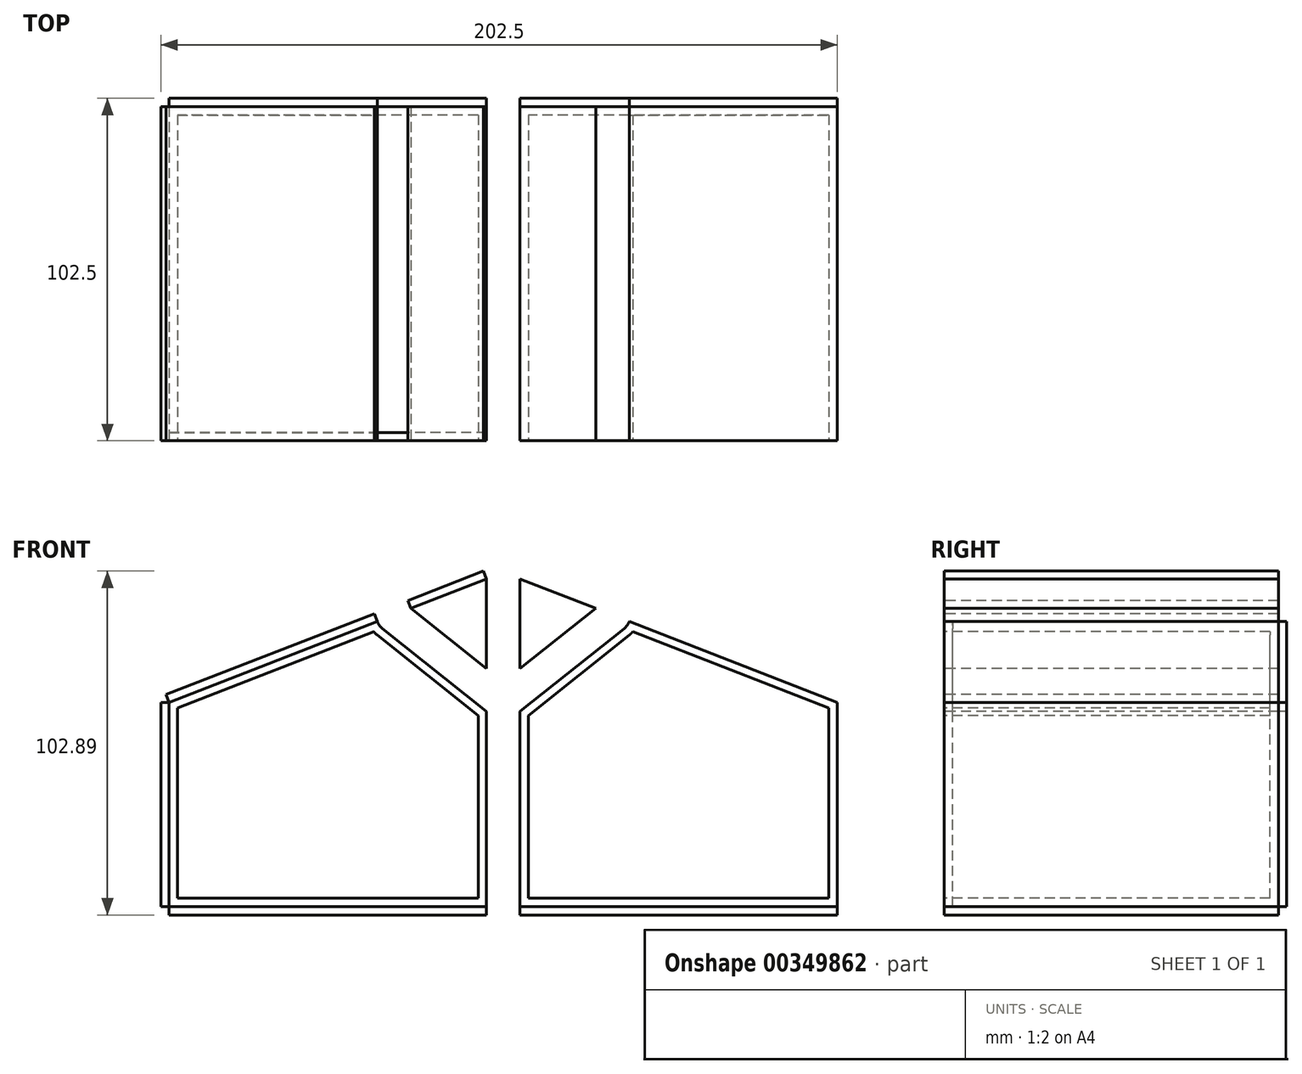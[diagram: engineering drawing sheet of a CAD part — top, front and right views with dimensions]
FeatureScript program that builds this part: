
annotation { "Feature Type Name" : "Feature", "Feature Type Description" : "" }
export const myFeature = defineFeature(function(context is Context, id is Id, definition is map)
    precondition{}
    {
        {
            var Q0;
            Q0=qCreatedBy(makeId("Front.planeOp"),FACE);
            var sketch = newSketch(context, id + "F0", { "sketchPlane" : qUnion([Q0])});
            skLineSegment(sketch, "E0", {"start": v(-100, 0) * mm, "end": v(-100, 61.13) * mm});
            skLineSegment(sketch, "E1", {"start": v(-100, 61.13) * mm, "end": v(0, 100) * mm});
            skLineSegment(sketch, "E2", {"start": v(0, 100) * mm, "end": v(100, 61.13) * mm});
            skLineSegment(sketch, "E3", {"start": v(100, 61.13) * mm, "end": v(100, 0) * mm});
            skLineSegment(sketch, "E4", {"start": v(100, 0) * mm, "end": v(-100, 0) * mm});
            skArc(sketch, "E5.0.endCap", {"start": v(-36.18, 83.24) * mm, "mid": v(-37.1, 84.18) * mm, "end": v(-37.72, 85.34) * mm});
            skLineSegment(sketch, "E5.0.left", {"start": v(-5, 58.4) * mm, "end": v(-36.18, 83.24) * mm});
            skArc(sketch, "E5.1.startCap", {"start": v(37.72, 85.34) * mm, "mid": v(37.1, 84.18) * mm, "end": v(36.18, 83.24) * mm});
            skLineSegment(sketch, "E5.1.left", {"start": v(36.18, 83.24) * mm, "end": v(5, 58.4) * mm});
            skLineSegment(sketch, "E5.1.right", {"start": v(27.67, 89.24) * mm, "end": v(5, 71.18) * mm});
            skLineSegment(sketch, "E5.2.left", {"start": v(-5, 0) * mm, "end": v(-5, 58.4) * mm});
            skLineSegment(sketch, "E5.2.right", {"start": v(5, 0) * mm, "end": v(5, 58.4) * mm});
            skLineSegment(sketch, "E6.trimOffspring", {"start": v(-5, 71.18) * mm, "end": v(-5, 98.06) * mm});
            skLineSegment(sketch, "E7.trimOffspring", {"start": v(-5, 71.18) * mm, "end": v(-27.67, 89.24) * mm});
            skLineSegment(sketch, "E8.trimOffspring", {"start": v(5, 71.18) * mm, "end": v(5, 98.06) * mm});
            skPoint(sketch, "E5.0.startCap.center.orphan", {"position": v(0, 60.8) * mm});
            skSolve(sketch);
        }
        {
            var Q0;
            {var subQ4=sQuery(id+"F0.wireOp",EDGE,"E5.0.endCap");Q0=makeQuery(id+"F0.imprint","IMPRINT",FACE,{"disambiguationData":[TD([[makeQuery(id+"F0.imprint","IMPRINT",EDGE,{"derivedFrom":subQ4}),-1.0]])]});}
            var Q1;
            {var subQ2=sQuery(id+"F0.wireOp",EDGE,"E0");Q1=makeQuery(id+"F0.imprint","IMPRINT",FACE,{"disambiguationData":[TD([[makeQuery(id+"F0.imprint","IMPRINT",EDGE,{"derivedFrom":subQ2}),-1.0]])]});}
            var Q2;
            {var subQ0=sQuery(id+"F0.wireOp",EDGE,"E6.trimOffspring");Q2=makeQuery(id+"F0.imprint","IMPRINT",FACE,{"disambiguationData":[TD([[makeQuery(id+"F0.imprint","IMPRINT",EDGE,{"derivedFrom":subQ0}),1.0]])]});}
            var Q3;
            {var subQ0=sQuery(id+"F0.wireOp",EDGE,"E5.1.right");Q3=makeQuery(id+"F0.imprint","IMPRINT",FACE,{"disambiguationData":[TD([[makeQuery(id+"F0.imprint","IMPRINT",EDGE,{"derivedFrom":subQ0}),-1.0]])]});}
            var Q4;
            {var subQ2=sQuery(id+"F0.wireOp",EDGE,"E3");Q4=makeQuery(id+"F0.imprint","IMPRINT",FACE,{"disambiguationData":[TD([[makeQuery(id+"F0.imprint","IMPRINT",EDGE,{"derivedFrom":subQ2}),-1.0]])]});}
            extrude(context, id + "F1", {"entities" : qUnion([Q0, Q1, Q2, Q3, Q4]), "oppositeDirection" : true, "depth" : 100 * mm});
        }
        {
            var Q0;
            Q0=makeQuery(id+"F1.opExtrude","CAP_FACE",FACE,{"disambiguationData":[OSD([sQuery(id+"F0.wireOp",EDGE,"E0"),sQuery(id+"F0.wireOp",EDGE,"E1"),sQuery(id+"F0.wireOp",EDGE,"E2"),sQuery(id+"F0.wireOp",EDGE,"E3"),sQuery(id+"F0.wireOp",EDGE,"E4")])],"isStart":true});
            shell(context, id + "F2", {"entities" : qUnion([Q0]), "thickness" : 2.5 * mm});
        }
        {
            var Q0;
            {var subQ4=sQuery(id+"F0.wireOp",EDGE,"E5.0.endCap");Q0=makeQuery(id+"F0.imprint","IMPRINT",FACE,{"disambiguationData":[TD([[makeQuery(id+"F0.imprint","IMPRINT",EDGE,{"derivedFrom":subQ4}),-1.0]])]});}
            extrude(context, id + "F3", {"entities" : qUnion([Q0]), "oppositeDirection" : true, "depth" : 2.5 * mm});
        }
        {
            var Q0;
            Q0=makeQuery(id+"F1.opExtrude","SWEPT_FACE",FACE,{"disambiguationData":[OSD([sQuery(id+"F0.wireOp",EDGE,"E0")])]});
            extrude(context, id + "F4", {"entities" : qUnion([Q0]), "depth" : 2.5 * mm});
        }
        {
            var Q0;
            Q0=makeQuery(id+"F1.opExtrude","SWEPT_FACE",FACE,{"disambiguationData":[OSD([sQuery(id+"F0.wireOp",EDGE,"E1")])]});
            extrude(context, id + "F5", {"entities" : qUnion([Q0]), "depth" : 2.5 * mm});
        }
        {
            var Q0;
            Q0=makeQuery(id+"F1.opExtrude","CAP_FACE",FACE,{"disambiguationData":[OSD([sQuery(id+"F0.wireOp",EDGE,"E0"),sQuery(id+"F0.wireOp",EDGE,"E1"),sQuery(id+"F0.wireOp",EDGE,"E2"),sQuery(id+"F0.wireOp",EDGE,"E3"),sQuery(id+"F0.wireOp",EDGE,"E4")])],"isStart":false});
            extrude(context, id + "F6", {"entities" : qUnion([Q0]), "depth" : 2.5 * mm});
        }
        {
            var Q0;
            Q0=makeQuery(id+"F1.opExtrude","SWEPT_FACE",FACE,{"disambiguationData":[OSD([sQuery(id+"F0.wireOp",EDGE,"E4")])]});
            extrude(context, id + "F7", {"entities" : qUnion([Q0]), "depth" : 2.5 * mm});
        }
    });
